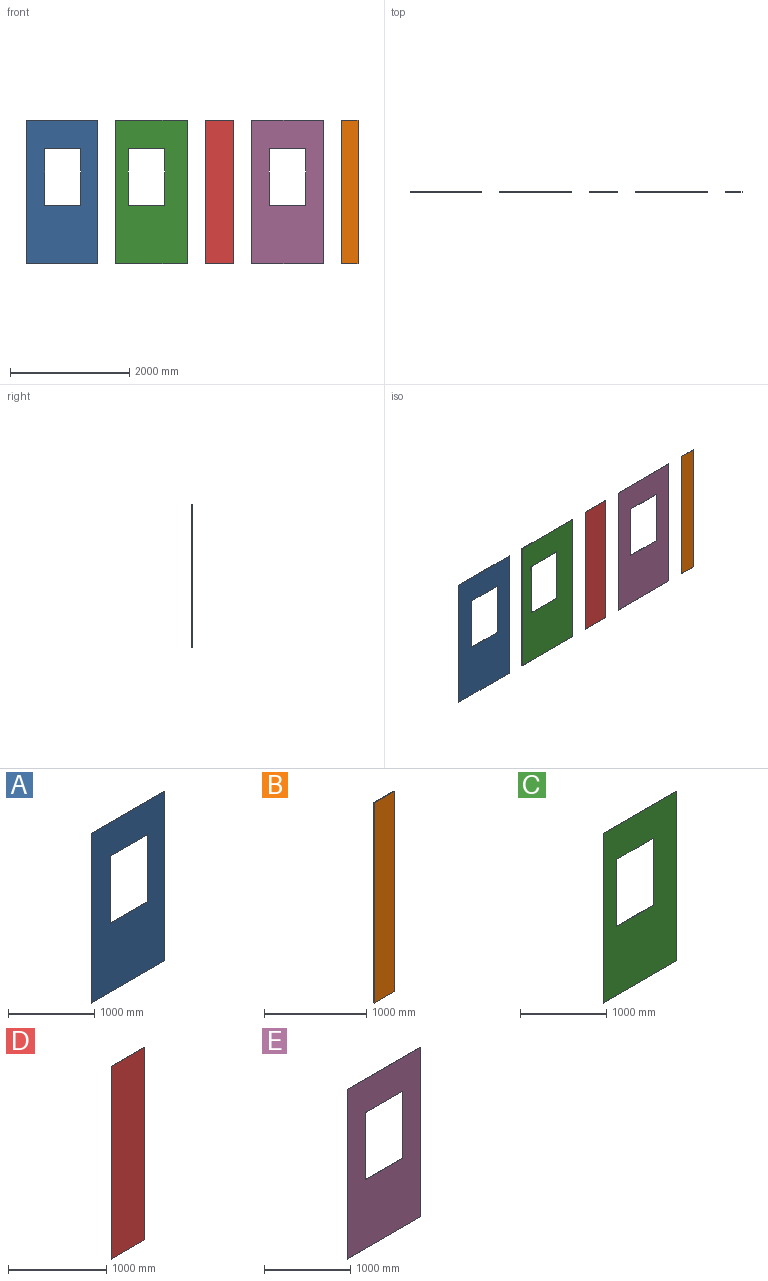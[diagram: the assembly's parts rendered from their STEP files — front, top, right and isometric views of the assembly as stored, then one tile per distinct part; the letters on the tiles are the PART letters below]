
ASSEMBLY  parts=5 mates=4
PART A: 10 faces, bbox 1200x5x2400 mm
  f0: plane 950x5mm, normal (1,0,0), area 4750mm2, adj f1,f7,f8,f9
  f1: plane 610x5mm, normal (0,0,-1), area 3050mm2, adj f0,f2,f8,f9
  f2: plane 950x5mm, normal (-1,0,0), area 4750mm2, adj f1,f7,f8,f9
  f3: plane 1200x5mm, normal (0,0,1), area 6000mm2, adj f4,f6,f8,f9
  f4: plane 2400x5mm, normal (-1,0,0), area 12000mm2, adj f3,f5,f8,f9
  f5: plane 1200x5mm, normal (0,0,-1), area 6000mm2, adj f4,f6,f8,f9
  f6: plane 2400x5mm, normal (1,0,0), area 12000mm2, adj f3,f5,f8,f9
  f7: plane 610x5mm, normal (0,0,1), area 3050mm2, adj f0,f2,f8,f9
  f8: plane 2400x1200mm, normal (0,-1,0), area 2300500mm2, adj f0,f1,f2,f3,f4,f5,f6,f7
  f9: plane 2400x1200mm, normal (0,1,0), area 2300500mm2, adj f0,f1,f2,f3,f4,f5,f6,f7
PART B: 6 faces, bbox 280x5x2400 mm
  f0: plane 280x5mm, normal (0,0,1), area 1400mm2, adj f1,f3,f4,f5
  f1: plane 2400x5mm, normal (-1,0,0), area 12000mm2, adj f0,f2,f4,f5
  f2: plane 280x5mm, normal (0,0,-1), area 1400mm2, adj f1,f3,f4,f5
  f3: plane 2400x5mm, normal (1,0,0), area 12000mm2, adj f0,f2,f4,f5
  f4: plane 2400x280mm, normal (0,-1,0), area 672000mm2, adj f0,f1,f2,f3
  f5: plane 2400x280mm, normal (0,1,0), area 672000mm2, adj f0,f1,f2,f3
PART C: 10 faces, bbox 1200x5x2400 mm
  f0: plane 950x5mm, normal (1,0,0), area 4750mm2, adj f1,f7,f8,f9
  f1: plane 605x5mm, normal (0,0,-1), area 3025mm2, adj f0,f2,f8,f9
  f2: plane 950x5mm, normal (-1,0,0), area 4750mm2, adj f1,f7,f8,f9
  f3: plane 2400x5mm, normal (1,0,0), area 12000mm2, adj f4,f6,f8,f9
  f4: plane 1200x5mm, normal (0,0,1), area 6000mm2, adj f3,f5,f8,f9
  f5: plane 2400x5mm, normal (-1,0,0), area 12000mm2, adj f4,f6,f8,f9
  f6: plane 1200x5mm, normal (0,0,-1), area 6000mm2, adj f3,f5,f8,f9
  f7: plane 605x5mm, normal (0,0,1), area 3025mm2, adj f0,f2,f8,f9
  f8: plane 2400x1200mm, normal (0,-1,0), area 2305250mm2, adj f0,f1,f2,f3,f4,f5,f6,f7
  f9: plane 2400x1200mm, normal (0,1,0), area 2305250mm2, adj f0,f1,f2,f3,f4,f5,f6,f7
PART D: 6 faces, bbox 480x5x2400 mm
  f0: plane 2400x5mm, normal (1,0,0), area 12000mm2, adj f1,f3,f4,f5
  f1: plane 480x5mm, normal (0,0,1), area 2400mm2, adj f0,f2,f4,f5
  f2: plane 2400x5mm, normal (-1,0,0), area 12000mm2, adj f1,f3,f4,f5
  f3: plane 480x5mm, normal (0,0,-1), area 2400mm2, adj f0,f2,f4,f5
  f4: plane 2400x480mm, normal (0,-1,0), area 1152000mm2, adj f0,f1,f2,f3
  f5: plane 2400x480mm, normal (0,1,0), area 1152000mm2, adj f0,f1,f2,f3
PART E: 10 faces, bbox 1200x5x2400 mm
  f0: plane 1200x5mm, normal (0,0,1), area 6000mm2, adj f1,f7,f8,f9
  f1: plane 2400x5mm, normal (-1,0,0), area 12000mm2, adj f0,f2,f8,f9
  f2: plane 1200x5mm, normal (0,0,-1), area 6000mm2, adj f1,f7,f8,f9
  f3: plane 950x5mm, normal (1,0,0), area 4750mm2, adj f4,f6,f8,f9
  f4: plane 610x5mm, normal (0,0,-1), area 3050mm2, adj f3,f5,f8,f9
  f5: plane 950x5mm, normal (-1,0,0), area 4750mm2, adj f4,f6,f8,f9
  f6: plane 610x5mm, normal (0,0,1), area 3050mm2, adj f3,f5,f8,f9
  f7: plane 2400x5mm, normal (1,0,0), area 12000mm2, adj f0,f2,f8,f9
  f8: plane 2400x1200mm, normal (0,-1,0), area 2300500mm2, adj f0,f1,f2,f3,f4,f5,f6,f7
  f9: plane 2400x1200mm, normal (0,1,0), area 2300500mm2, adj f0,f1,f2,f3,f4,f5,f6,f7
PLACE A t=(129.96,0,43.18)mm
PLACE B t=(1064.96,0,43.18)mm
PLACE C t=(194.96,0,43.18)mm
PLACE D t=(474.96,0,43.18)mm
PLACE E t=(769.96,0,43.18)mm
MATE fastened C.f8 <-> D.f4  axis (0,-1,0) through (2829.96,-535,2683.18)mm
MATE fastened A.f8 <-> C.f8  axis (0,-1,0) through (1329.96,-535,2683.18)mm
MATE fastened D.f4 <-> E.f8  axis (0,-1,0) through (3609.96,-535,2683.18)mm
MATE fastened E.f8 <-> B.f4  axis (0,-1,0) through (5109.96,-535,2683.18)mm
